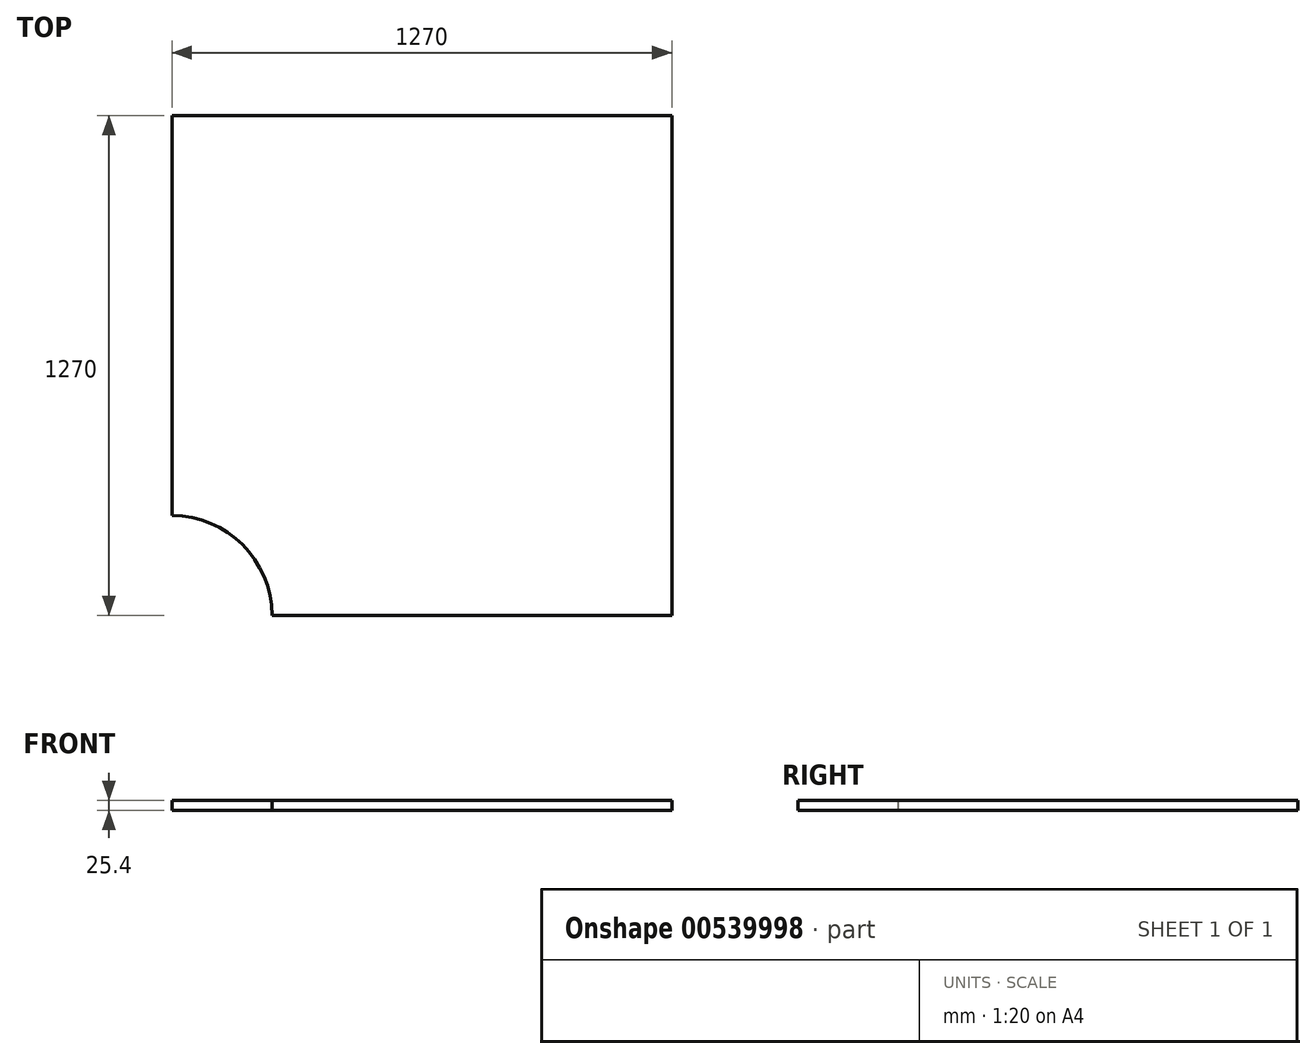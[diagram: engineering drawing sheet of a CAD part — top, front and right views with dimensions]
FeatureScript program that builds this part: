
annotation { "Feature Type Name" : "Feature", "Feature Type Description" : "" }
export const myFeature = defineFeature(function(context is Context, id is Id, definition is map)
    precondition{}
    {
        {
            var Q0;
            Q0=qCreatedBy(makeId("Top.planeOp"),FACE);
            var sketch = newSketch(context, id + "F0", { "sketchPlane" : qUnion([Q0])});
            skLineSegment(sketch, "E0.bottom", {"start": v(0, 0) * mm, "end": v(1270, 0) * mm});
            skLineSegment(sketch, "E0.top", {"start": v(0, 1270) * mm, "end": v(1270, 1270) * mm});
            skLineSegment(sketch, "E0.left", {"start": v(0, 0) * mm, "end": v(0, 1270) * mm});
            skLineSegment(sketch, "E0.right", {"start": v(1270, 0) * mm, "end": v(1270, 1270) * mm});
            skCircle(sketch, "E1", {"center": v(0, 0) * mm, "radius": 254 * mm});
            skSolve(sketch);
        }
        {
            var Q0;
            {var subQ2=sQuery(id+"F0.wireOp",EDGE,"E0.top");Q0=makeQuery(id+"F0.imprint","IMPRINT",FACE,{"disambiguationData":[TD([[makeQuery(id+"F0.imprint","IMPRINT",EDGE,{"derivedFrom":subQ2}),-1.0]])]});}
            extrude(context, id + "F1", {"entities" : qUnion([Q0]), "depth" : 25.4 * mm, "offsetDistance" : 25.4 * mm});
        }
    });
